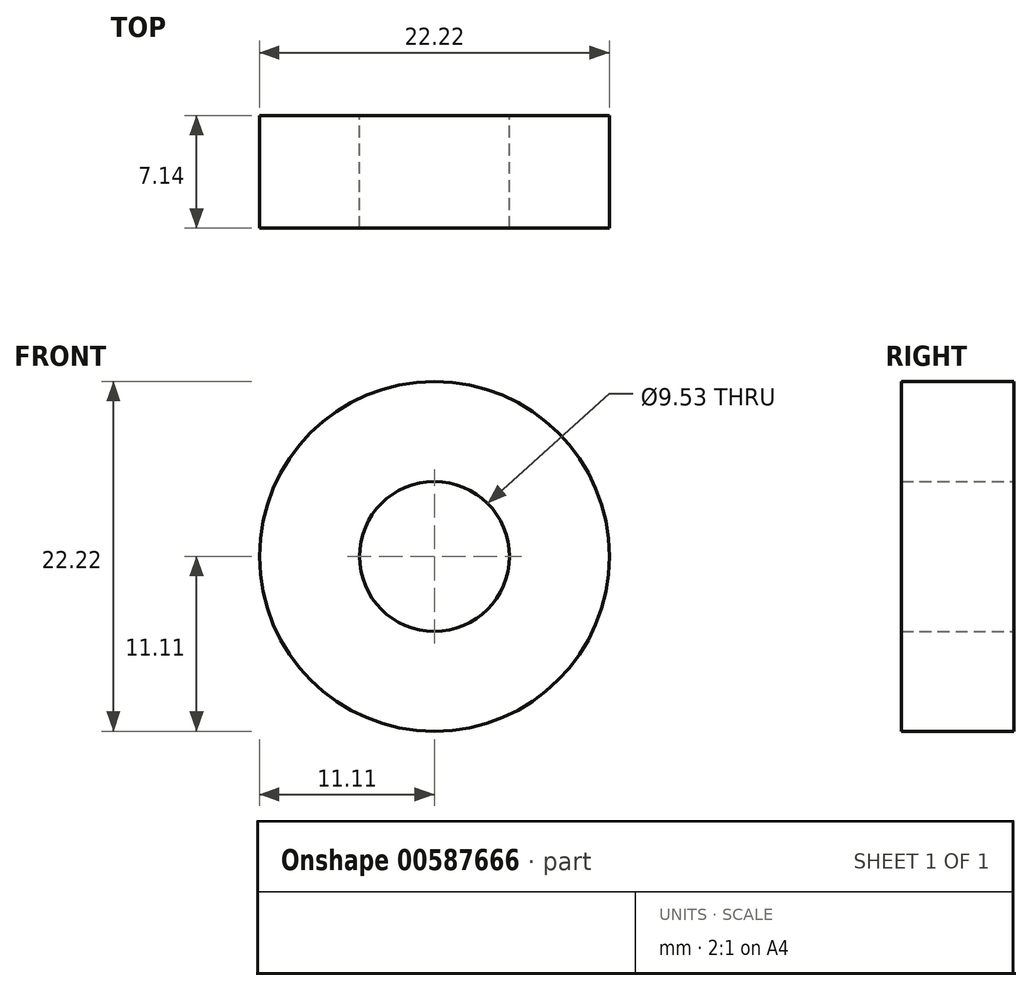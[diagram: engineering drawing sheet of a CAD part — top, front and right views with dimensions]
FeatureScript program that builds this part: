
annotation { "Feature Type Name" : "Feature", "Feature Type Description" : "" }
export const myFeature = defineFeature(function(context is Context, id is Id, definition is map)
    precondition{}
    {
        {
            var Q0;
            Q0=qCreatedBy(makeId("Front.planeOp"),FACE);
            var sketch = newSketch(context, id + "F0", { "sketchPlane" : qUnion([Q0])});
            skCircle(sketch, "E0", {"center": v(0, 0) * mm, "radius": 11.11 * mm});
            skCircle(sketch, "E1", {"center": v(0, 0) * mm, "radius": 4.76 * mm});
            skSolve(sketch);
        }
        {
            var Q0;
            Q0 = qSketchRegion(id + "F0", true);
            extrude(context, id + "F1", {"entities" : qUnion([Q0]), "endBound" : BoundingType.SYMMETRIC, "depth" : 7.14 * mm, "offsetDistance" : 25.4 * mm});
        }
    });
